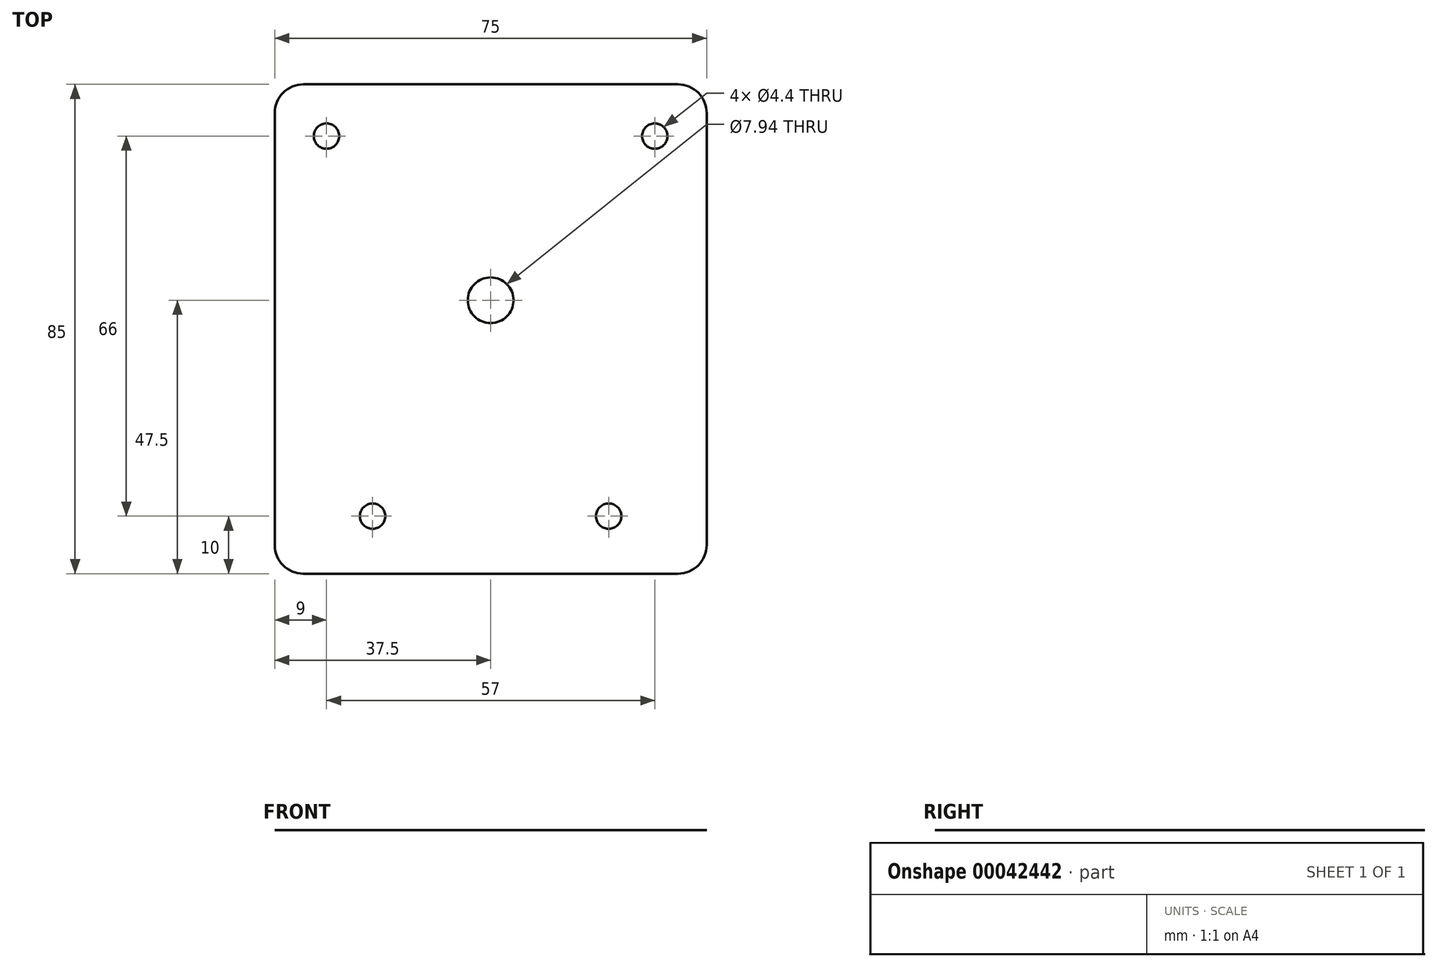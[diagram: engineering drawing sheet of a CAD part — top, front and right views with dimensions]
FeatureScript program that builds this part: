
annotation { "Feature Type Name" : "Feature", "Feature Type Description" : "" }
export const myFeature = defineFeature(function(context is Context, id is Id, definition is map)
    precondition{}
    {
        {
            var Q0;
            Q0=qCreatedBy(makeId("Top.planeOp"),FACE);
            var sketch = newSketch(context, id + "F0", { "sketchPlane" : qUnion([Q0])});
            skLineSegment(sketch, "E0.bottom", {"start": v(0, 0) * mm, "end": v(75, 0) * mm});
            skLineSegment(sketch, "E0.top", {"start": v(0, 85) * mm, "end": v(75, 85) * mm});
            skLineSegment(sketch, "E0.left", {"start": v(0, 0) * mm, "end": v(0, 85) * mm});
            skLineSegment(sketch, "E0.right", {"start": v(75, 0) * mm, "end": v(75, 85) * mm});
            skCircle(sketch, "E1", {"center": v(9, 76) * mm, "radius": 2.2 * mm});
            skCircle(sketch, "E2", {"center": v(17, 10) * mm, "radius": 2.2 * mm});
            skLineSegment(sketch, "E3", {"start": v(37.5, 85) * mm, "end": v(37.5, 0) * mm, "construction": true});
            skCircle(sketch, "E4", {"center": v(37.5, 47.5) * mm, "radius": 3.97 * mm});
            skLineSegment(sketch, "E5", {"start": v(37.5, 47.5) * mm, "end": v(37.5, 85) * mm, "construction": true});
            skLineSegment(sketch, "E6", {"start": v(37.5, 47.5) * mm, "end": v(0, 47.5) * mm, "construction": true});
            skCircle(sketch, "E7.0.MirrorC", {"center": v(58, 10) * mm, "radius": 2.2 * mm});
            skCircle(sketch, "E8.0.MirrorC", {"center": v(66, 76) * mm, "radius": 2.2 * mm});
            skSolve(sketch);
        }
        {
            var Q0;
            Q0=qSketchRegion(id+"F0",true);
            extrude(context, id + "F1", {"entities" : qUnion([Q0]), "depth" : 1 / 203.2 * mm});
        }
        {
            var Q0;
            Q0=makeQuery(id+"F1.opExtrude","SWEPT_EDGE",EDGE,{"disambiguationData":[OSD([sQuery(id+"F0.wireOp",EDGE,"E0.bottom"),sQuery(id+"F0.wireOp",EDGE,"E0.left")])]});
            var Q1;
            Q1=makeQuery(id+"F1.opExtrude","SWEPT_EDGE",EDGE,{"disambiguationData":[OSD([sQuery(id+"F0.wireOp",EDGE,"E0.top"),sQuery(id+"F0.wireOp",EDGE,"E0.right")])]});
            var Q2;
            Q2=makeQuery(id+"F1.opExtrude","SWEPT_EDGE",EDGE,{"disambiguationData":[OSD([sQuery(id+"F0.wireOp",EDGE,"E0.bottom"),sQuery(id+"F0.wireOp",EDGE,"E0.right")])]});
            var Q3;
            Q3=makeQuery(id+"F1.opExtrude","SWEPT_EDGE",EDGE,{"disambiguationData":[OSD([sQuery(id+"F0.wireOp",EDGE,"E0.top"),sQuery(id+"F0.wireOp",EDGE,"E0.left")])]});
            fillet(context, id + "F2", {"entities" : qUnion([Q0, Q1, Q2, Q3]), "radius" : 5 * mm, "tangentPropagation" : true, "allowEdgeOverflow" : false});
        }
    });
